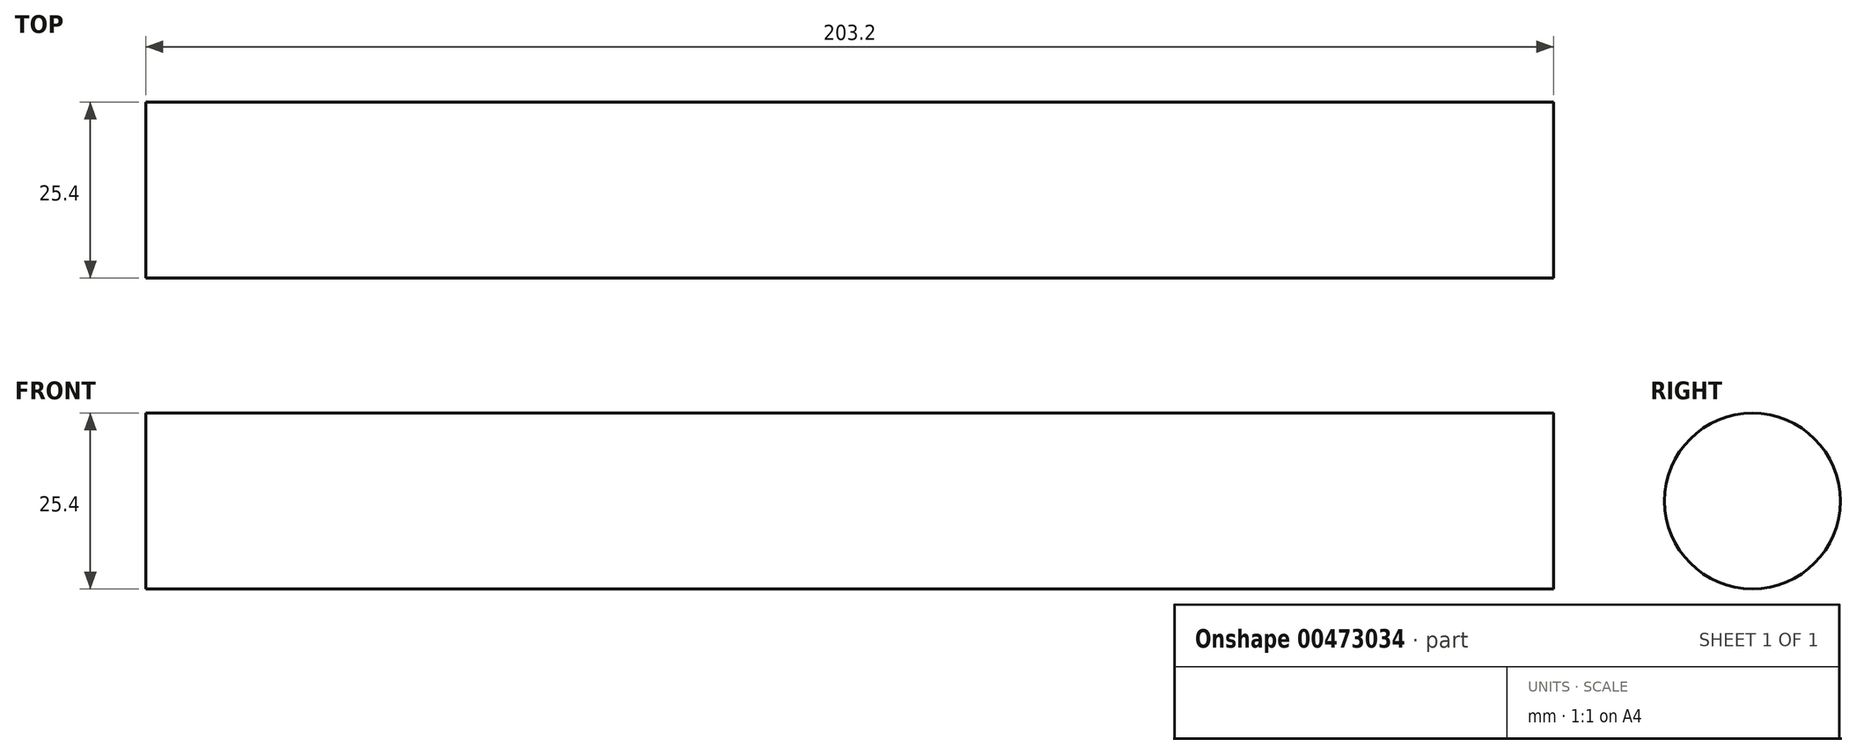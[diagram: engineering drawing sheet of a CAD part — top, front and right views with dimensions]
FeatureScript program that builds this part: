
annotation { "Feature Type Name" : "Feature", "Feature Type Description" : "" }
export const myFeature = defineFeature(function(context is Context, id is Id, definition is map)
    precondition{}
    {
        {
            var Q0;
            Q0=qCreatedBy(makeId("Right.planeOp"),FACE);
            var sketch = newSketch(context, id + "F0", { "sketchPlane" : qUnion([Q0])});
            skCircle(sketch, "E0", {"center": v(0, 0) * mm, "radius": 12.7 * mm});
            skSolve(sketch);
        }
        {
            var Q0;
            Q0 = qSketchRegion(id + "F0", true);
            var Q1;
            Q1=makeQuery(id+"F0.imprint","IMPRINT",FACE,{"disambiguationData":[TD([[makeQuery(id+"F0.imprint","IMPRINT",EDGE,{"derivedFrom":sQuery(id+"F0.wireOp",EDGE,"E0")}),1.0]])]});
            extrude(context, id + "F1", {"entities" : qUnion([Q0, Q1]), "depth" : 203.2 * mm});
        }
    });
